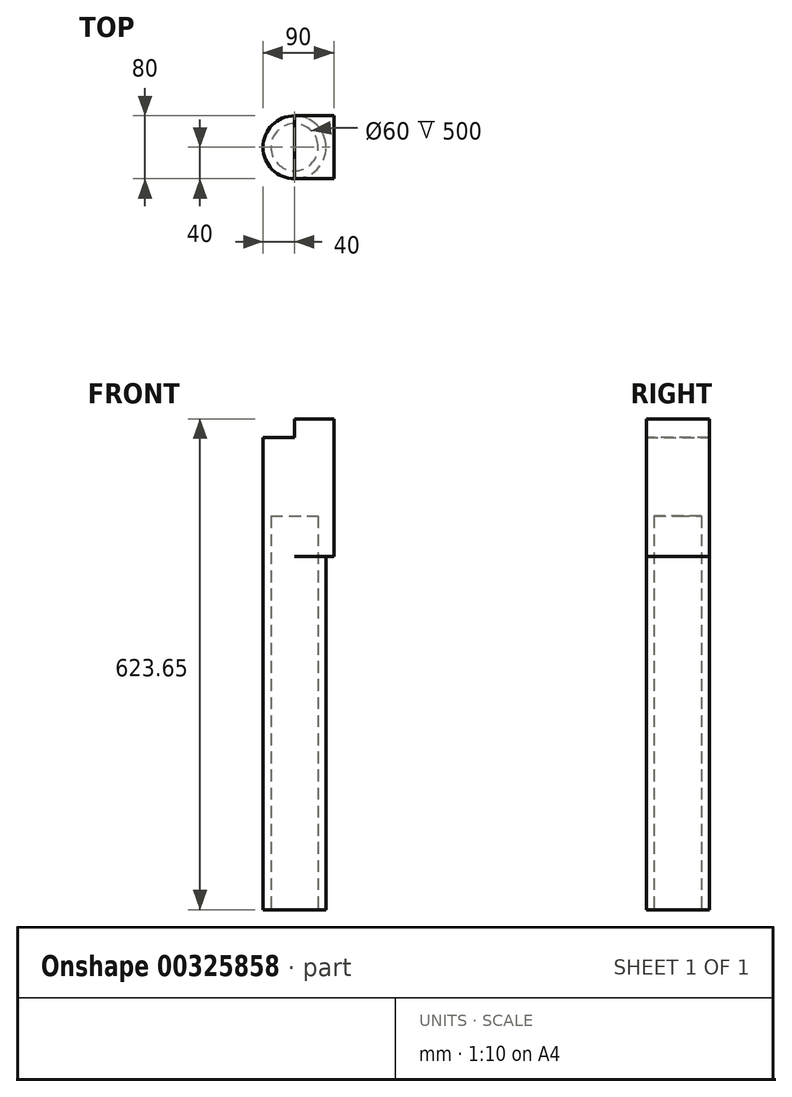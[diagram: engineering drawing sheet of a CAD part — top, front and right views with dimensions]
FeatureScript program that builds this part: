
annotation { "Feature Type Name" : "Feature", "Feature Type Description" : "" }
export const myFeature = defineFeature(function(context is Context, id is Id, definition is map)
    precondition{}
    {
        {
            var Q0;
            Q0=qCreatedBy(makeId("Top.planeOp"),FACE);
            var sketch = newSketch(context, id + "F0", { "sketchPlane" : qUnion([Q0])});
            skCircle(sketch, "E0", {"center": v(0, 0) * mm, "radius": 40 * mm});
            skSolve(sketch);
        }
        {
            var Q0;
            Q0=makeQuery(id+"F0.imprint","IMPRINT",FACE,{"disambiguationData":[TD([[makeQuery(id+"F0.imprint","IMPRINT",EDGE,{"derivedFrom":sQuery(id+"F0.wireOp",EDGE,"E0")}),1.0]])]});
            extrude(context, id + "F1", {"entities" : qUnion([Q0]), "depth" : 600 * mm});
        }
        {
            var Q0;
            Q0=qCreatedBy(makeId("Front.planeOp"),FACE);
            var sketch = newSketch(context, id + "F2", { "sketchPlane" : qUnion([Q0])});
            skLineSegment(sketch, "E1.bottom", {"start": v(0, 623.65) * mm, "end": v(50, 623.65) * mm});
            skLineSegment(sketch, "E1.top", {"start": v(0, 448.65) * mm, "end": v(50, 448.65) * mm});
            skLineSegment(sketch, "E1.left", {"start": v(0, 623.65) * mm, "end": v(0, 448.65) * mm});
            skLineSegment(sketch, "E1.right", {"start": v(50, 623.65) * mm, "end": v(50, 448.65) * mm});
            skSolve(sketch);
        }
        {
            var Q0;
            Q0=makeQuery(id+"F2.imprint","IMPRINT",FACE,{"disambiguationData":[TD([[makeQuery(id+"F2.imprint","IMPRINT",EDGE,{"derivedFrom":sQuery(id+"F2.wireOp",EDGE,"E1.bottom")}),-1.0]])]});
            extrude(context, id + "F3", {"entities" : qUnion([Q0]), "operationType" : NewBodyOperationType.ADD, "endBound" : BoundingType.SYMMETRIC, "depth" : 80 * mm});
        }
        {
            var Q0;
            Q0=makeQuery(id+"F1.opExtrude","CAP_FACE",FACE,{"disambiguationData":[OSD([sQuery(id+"F0.wireOp",EDGE,"E0")])],"isStart":true});
            var sketch = newSketch(context, id + "F4", { "sketchPlane" : qUnion([Q0])});
            skCircle(sketch, "E2", {"center": v(0, 0) * mm, "radius": 30 * mm});
            skSolve(sketch);
        }
        {
            var Q0;
            Q0=makeQuery(id+"F4.imprint","IMPRINT",FACE,{"disambiguationData":[TD([[makeQuery(id+"F4.imprint","IMPRINT",EDGE,{"derivedFrom":sQuery(id+"F4.wireOp",EDGE,"E2")}),1.0]])]});
            extrude(context, id + "F5", {"entities" : qUnion([Q0]), "operationType" : NewBodyOperationType.REMOVE, "oppositeDirection" : true, "depth" : 500 * mm});
        }
    });
